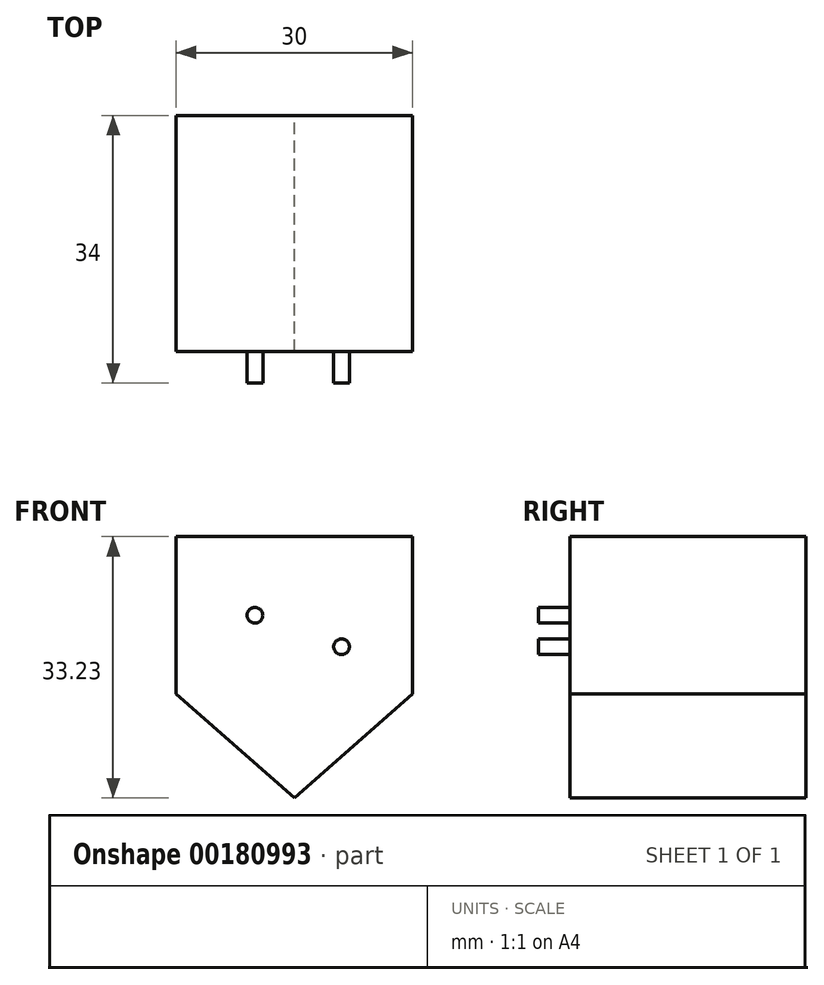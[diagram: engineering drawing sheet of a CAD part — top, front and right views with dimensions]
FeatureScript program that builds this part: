
annotation { "Feature Type Name" : "Feature", "Feature Type Description" : "" }
export const myFeature = defineFeature(function(context is Context, id is Id, definition is map)
    precondition{}
    {
        {
            var Q0;
            Q0=qCreatedBy(makeId("Front.planeOp"),FACE);
            var sketch = newSketch(context, id + "F0", { "sketchPlane" : qUnion([Q0])});
            skLineSegment(sketch, "E0", {"start": v(0, 0) * mm, "end": v(15, 0) * mm});
            skLineSegment(sketch, "E1", {"start": v(15, 0) * mm, "end": v(15, 20) * mm});
            skLineSegment(sketch, "E2", {"start": v(15, 20) * mm, "end": v(0, 20) * mm});
            skLineSegment(sketch, "E3", {"start": v(0, 20) * mm, "end": v(-15, 20) * mm});
            skLineSegment(sketch, "E4", {"start": v(-15, 20) * mm, "end": v(-15, 0) * mm});
            skLineSegment(sketch, "E5", {"start": v(-15, 0) * mm, "end": v(0, -13.23) * mm});
            skLineSegment(sketch, "E6", {"start": v(0, -13.23) * mm, "end": v(15, 0) * mm});
            skSolve(sketch);
        }
        {
            var Q0;
            Q0 = qSketchRegion(id + "F0", true);
            extrude(context, id + "F1", {"entities" : qUnion([Q0]), "depth" : 10 * mm, "hasSecondDirection" : true, "secondDirectionOppositeDirection" : true, "secondDirectionDepth" : 20 * mm});
        }
        {
            var Q0;
            Q0=makeQuery(id+"F1.opExtrude","CAP_FACE",FACE,{"disambiguationData":[OSD([sQuery(id+"F0.wireOp",EDGE,"E1"),sQuery(id+"F0.wireOp",EDGE,"E2"),sQuery(id+"F0.wireOp",EDGE,"E3"),sQuery(id+"F0.wireOp",EDGE,"E4"),sQuery(id+"F0.wireOp",EDGE,"E5"),sQuery(id+"F0.wireOp",EDGE,"E6")])],"isStart":false});
            var sketch = newSketch(context, id + "F2", { "sketchPlane" : qUnion([Q0])});
            skCircle(sketch, "E7", {"center": v(-5, 10) * mm, "radius": 1 * mm});
            skCircle(sketch, "E8", {"center": v(6, 6) * mm, "radius": 1 * mm});
            skSolve(sketch);
        }
        {
            var Q0;
            Q0 = qSketchRegion(id + "F2", true);
            extrude(context, id + "F3", {"entities" : qUnion([Q0]), "operationType" : NewBodyOperationType.ADD, "depth" : 4 * mm});
        }
    });
